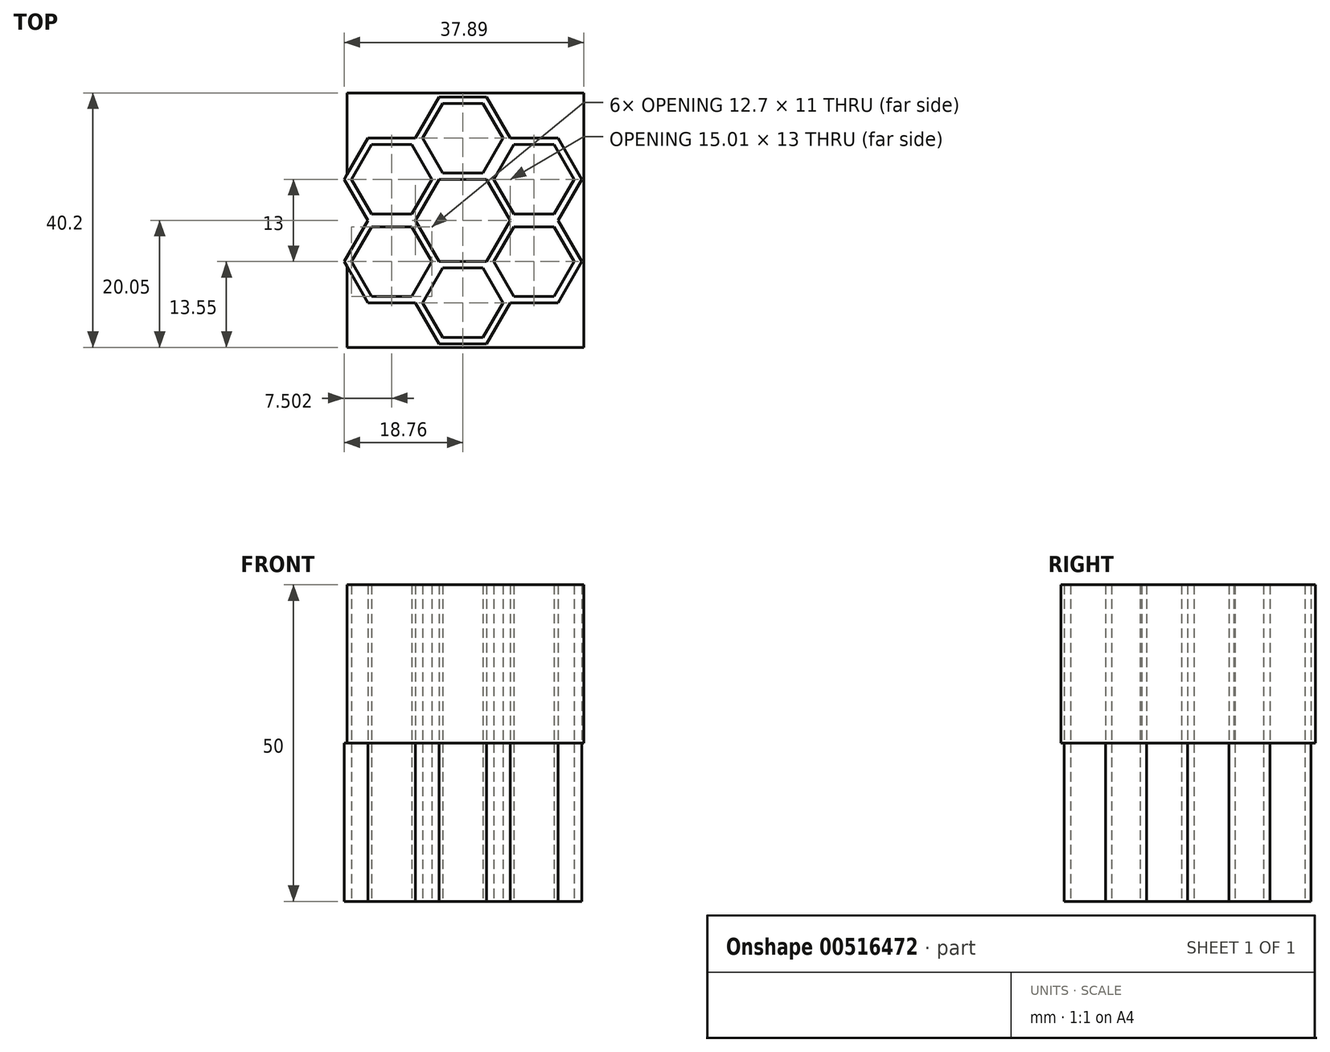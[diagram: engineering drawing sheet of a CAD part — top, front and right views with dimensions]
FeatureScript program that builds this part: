
annotation { "Feature Type Name" : "Feature", "Feature Type Description" : "" }
export const myFeature = defineFeature(function(context is Context, id is Id, definition is map)
    precondition{}
    {
        {
            var Q0;
            Q0=qCreatedBy(makeId("Top.planeOp"),FACE);
            var sketch = newSketch(context, id + "F0", { "sketchPlane" : qUnion([Q0])});
            skLineSegment(sketch, "E0.0", {"start": v(-3.75, 6.5) * mm, "end": v(3.75, 6.5) * mm});
            skLineSegment(sketch, "E0.1", {"start": v(3.75, 6.5) * mm, "end": v(7.5, 0) * mm});
            skLineSegment(sketch, "E0.2", {"start": v(7.5, 0) * mm, "end": v(3.75, -6.5) * mm});
            skLineSegment(sketch, "E0.3", {"start": v(3.75, -6.5) * mm, "end": v(-3.75, -6.5) * mm});
            skLineSegment(sketch, "E0.4", {"start": v(-3.75, -6.5) * mm, "end": v(-7.5, 0) * mm});
            skLineSegment(sketch, "E0.5", {"start": v(-7.5, 0) * mm, "end": v(-3.75, 6.5) * mm});
            skPoint(sketch, "E0.0.midPoint", {"position": v(0, 6.5) * mm});
            skLineSegment(sketch, "E1.0", {"start": v(7.5, 0) * mm, "end": v(15.01, 0) * mm});
            skLineSegment(sketch, "E1.1", {"start": v(15.01, 0) * mm, "end": v(18.76, -6.5) * mm});
            skLineSegment(sketch, "E1.2", {"start": v(18.76, -6.5) * mm, "end": v(15.01, -13) * mm});
            skLineSegment(sketch, "E1.3", {"start": v(15.01, -13) * mm, "end": v(7.5, -13) * mm});
            skLineSegment(sketch, "E1.4", {"start": v(7.5, -13) * mm, "end": v(3.75, -6.5) * mm});
            skLineSegment(sketch, "E1.5", {"start": v(3.75, -6.5) * mm, "end": v(7.5, 0) * mm});
            skPoint(sketch, "E1.0.midPoint", {"position": v(11.26, 0) * mm});
            skLineSegment(sketch, "E2.0", {"start": v(7.5, 13) * mm, "end": v(15.01, 13) * mm});
            skLineSegment(sketch, "E2.1", {"start": v(15.01, 13) * mm, "end": v(18.76, 6.5) * mm});
            skLineSegment(sketch, "E2.2", {"start": v(18.76, 6.5) * mm, "end": v(15.01, 0) * mm});
            skLineSegment(sketch, "E2.3", {"start": v(15.01, 0) * mm, "end": v(7.5, 0) * mm});
            skLineSegment(sketch, "E2.4", {"start": v(7.5, 0) * mm, "end": v(3.75, 6.5) * mm});
            skLineSegment(sketch, "E2.5", {"start": v(3.75, 6.5) * mm, "end": v(7.5, 13) * mm});
            skPoint(sketch, "E2.0.midPoint", {"position": v(11.26, 13) * mm});
            skLineSegment(sketch, "E3.0", {"start": v(-3.75, 19.5) * mm, "end": v(3.75, 19.5) * mm});
            skLineSegment(sketch, "E3.1", {"start": v(3.75, 19.5) * mm, "end": v(7.5, 13) * mm});
            skLineSegment(sketch, "E3.2", {"start": v(7.5, 13) * mm, "end": v(3.75, 6.5) * mm});
            skLineSegment(sketch, "E3.3", {"start": v(3.75, 6.5) * mm, "end": v(-3.75, 6.5) * mm});
            skLineSegment(sketch, "E3.4", {"start": v(-3.75, 6.5) * mm, "end": v(-7.5, 13) * mm});
            skLineSegment(sketch, "E3.5", {"start": v(-7.5, 13) * mm, "end": v(-3.75, 19.5) * mm});
            skPoint(sketch, "E3.0.midPoint", {"position": v(0, 19.5) * mm});
            skLineSegment(sketch, "E4.0", {"start": v(-15.01, 13) * mm, "end": v(-7.5, 13) * mm});
            skLineSegment(sketch, "E4.1", {"start": v(-7.5, 13) * mm, "end": v(-3.75, 6.5) * mm});
            skLineSegment(sketch, "E4.2", {"start": v(-3.75, 6.5) * mm, "end": v(-7.5, 0) * mm});
            skLineSegment(sketch, "E4.3", {"start": v(-7.5, 0) * mm, "end": v(-15.01, 0) * mm});
            skLineSegment(sketch, "E4.4", {"start": v(-15.01, 0) * mm, "end": v(-18.76, 6.5) * mm});
            skLineSegment(sketch, "E4.5", {"start": v(-18.76, 6.5) * mm, "end": v(-15.01, 13) * mm});
            skPoint(sketch, "E4.0.midPoint", {"position": v(-11.26, 13) * mm});
            skLineSegment(sketch, "E5.0", {"start": v(-15.01, 0) * mm, "end": v(-7.5, 0) * mm});
            skLineSegment(sketch, "E5.1", {"start": v(-7.5, 0) * mm, "end": v(-3.75, -6.5) * mm});
            skLineSegment(sketch, "E5.2", {"start": v(-3.75, -6.5) * mm, "end": v(-7.5, -13) * mm});
            skLineSegment(sketch, "E5.3", {"start": v(-7.5, -13) * mm, "end": v(-15.01, -13) * mm});
            skLineSegment(sketch, "E5.4", {"start": v(-15.01, -13) * mm, "end": v(-18.76, -6.5) * mm});
            skLineSegment(sketch, "E5.5", {"start": v(-18.76, -6.5) * mm, "end": v(-15.01, 0) * mm});
            skPoint(sketch, "E5.0.midPoint", {"position": v(-11.26, 0) * mm});
            skLineSegment(sketch, "E6.0", {"start": v(-3.75, -6.5) * mm, "end": v(3.75, -6.5) * mm});
            skLineSegment(sketch, "E6.1", {"start": v(3.75, -6.5) * mm, "end": v(7.5, -13) * mm});
            skLineSegment(sketch, "E6.2", {"start": v(7.5, -13) * mm, "end": v(3.75, -19.5) * mm});
            skLineSegment(sketch, "E6.3", {"start": v(3.75, -19.5) * mm, "end": v(-3.75, -19.5) * mm});
            skLineSegment(sketch, "E6.4", {"start": v(-3.75, -19.5) * mm, "end": v(-7.5, -13) * mm});
            skLineSegment(sketch, "E6.5", {"start": v(-7.5, -13) * mm, "end": v(-3.75, -6.5) * mm});
            skPoint(sketch, "E6.0.midPoint", {"position": v(0, -6.5) * mm});
            skLineSegment(sketch, "E7.0", {"start": v(-14.43, 1) * mm, "end": v(-17.6, 6.5) * mm});
            skLineSegment(sketch, "E7.1", {"start": v(-14.43, 12) * mm, "end": v(-8.08, 12) * mm});
            skLineSegment(sketch, "E7.2", {"start": v(-4.9, 6.5) * mm, "end": v(-8.08, 12) * mm});
            skLineSegment(sketch, "E7.3", {"start": v(-17.6, 6.5) * mm, "end": v(-14.43, 12) * mm});
            skLineSegment(sketch, "E7.4", {"start": v(-8.08, 1) * mm, "end": v(-4.9, 6.5) * mm});
            skLineSegment(sketch, "E7.5", {"start": v(-14.43, 1) * mm, "end": v(-8.08, 1) * mm});
            skLineSegment(sketch, "E8.0", {"start": v(-17.6, -6.5) * mm, "end": v(-14.43, -1) * mm});
            skLineSegment(sketch, "E8.1", {"start": v(-8.08, -1) * mm, "end": v(-4.9, -6.5) * mm});
            skLineSegment(sketch, "E8.2", {"start": v(-8.08, -12) * mm, "end": v(-4.9, -6.5) * mm});
            skLineSegment(sketch, "E8.3", {"start": v(-14.43, -1) * mm, "end": v(-8.08, -1) * mm});
            skLineSegment(sketch, "E8.4", {"start": v(-8.08, -12) * mm, "end": v(-14.43, -12) * mm});
            skLineSegment(sketch, "E8.5", {"start": v(-14.43, -12) * mm, "end": v(-17.6, -6.5) * mm});
            skLineSegment(sketch, "E9.0", {"start": v(6.35, 0) * mm, "end": v(3.18, 5.5) * mm});
            skLineSegment(sketch, "E9.1", {"start": v(-6.35, 0) * mm, "end": v(-3.18, 5.5) * mm});
            skLineSegment(sketch, "E9.2", {"start": v(-6.35, 0) * mm, "end": v(-3.18, -5.5) * mm});
            skLineSegment(sketch, "E9.3", {"start": v(3.18, 5.5) * mm, "end": v(-3.18, 5.5) * mm});
            skLineSegment(sketch, "E9.4", {"start": v(-3.18, -5.5) * mm, "end": v(3.18, -5.5) * mm});
            skLineSegment(sketch, "E9.5", {"start": v(3.18, -5.5) * mm, "end": v(6.35, 0) * mm});
            skLineSegment(sketch, "E10.0", {"start": v(-6.35, 13) * mm, "end": v(-3.18, 18.5) * mm});
            skLineSegment(sketch, "E10.1", {"start": v(3.18, 18.5) * mm, "end": v(6.35, 13) * mm});
            skLineSegment(sketch, "E10.2", {"start": v(3.18, 7.5) * mm, "end": v(6.35, 13) * mm});
            skLineSegment(sketch, "E10.3", {"start": v(-3.18, 18.5) * mm, "end": v(3.18, 18.5) * mm});
            skLineSegment(sketch, "E10.4", {"start": v(3.18, 7.5) * mm, "end": v(-3.18, 7.5) * mm});
            skLineSegment(sketch, "E10.5", {"start": v(-3.18, 7.5) * mm, "end": v(-6.35, 13) * mm});
            skLineSegment(sketch, "E11.0", {"start": v(-3.18, -18.5) * mm, "end": v(-6.35, -13) * mm});
            skLineSegment(sketch, "E11.1", {"start": v(3.18, -7.5) * mm, "end": v(-3.18, -7.5) * mm});
            skLineSegment(sketch, "E11.2", {"start": v(6.35, -13) * mm, "end": v(3.18, -7.5) * mm});
            skLineSegment(sketch, "E11.3", {"start": v(-6.35, -13) * mm, "end": v(-3.18, -7.5) * mm});
            skLineSegment(sketch, "E11.4", {"start": v(6.35, -13) * mm, "end": v(3.18, -18.5) * mm});
            skLineSegment(sketch, "E11.5", {"start": v(3.18, -18.5) * mm, "end": v(-3.18, -18.5) * mm});
            skLineSegment(sketch, "E12.0", {"start": v(4.9, 6.5) * mm, "end": v(8.08, 12) * mm});
            skLineSegment(sketch, "E12.1", {"start": v(14.43, 12) * mm, "end": v(17.6, 6.5) * mm});
            skLineSegment(sketch, "E12.2", {"start": v(17.6, 6.5) * mm, "end": v(14.43, 1) * mm});
            skLineSegment(sketch, "E12.3", {"start": v(8.08, 12) * mm, "end": v(14.43, 12) * mm});
            skLineSegment(sketch, "E12.4", {"start": v(8.08, 1) * mm, "end": v(14.43, 1) * mm});
            skLineSegment(sketch, "E12.5", {"start": v(8.08, 1) * mm, "end": v(4.9, 6.5) * mm});
            skLineSegment(sketch, "E13.0", {"start": v(4.9, -6.5) * mm, "end": v(8.08, -1) * mm});
            skLineSegment(sketch, "E13.1", {"start": v(14.43, -1) * mm, "end": v(17.6, -6.5) * mm});
            skLineSegment(sketch, "E13.2", {"start": v(17.6, -6.5) * mm, "end": v(14.43, -12) * mm});
            skLineSegment(sketch, "E13.3", {"start": v(8.08, -1) * mm, "end": v(14.43, -1) * mm});
            skLineSegment(sketch, "E13.4", {"start": v(14.43, -12) * mm, "end": v(8.08, -12) * mm});
            skLineSegment(sketch, "E13.5", {"start": v(8.08, -12) * mm, "end": v(4.9, -6.5) * mm});
            skSolve(sketch);
        }
        {
            var Q0;
            Q0=qSketchRegion(id+"F0",true);
            extrude(context, id + "F1", {"entities" : qUnion([Q0]), "depth" : 25 * mm, "offsetDistance" : 25 * mm});
        }
        {
            var Q0;
            Q0=makeQuery(id+"F1.opExtrude","CAP_FACE",FACE,{"disambiguationData":[OSD([sQuery(id+"F0.wireOp",EDGE,"E1.1"),sQuery(id+"F0.wireOp",EDGE,"E1.2"),sQuery(id+"F0.wireOp",EDGE,"E1.3"),sQuery(id+"F0.wireOp",EDGE,"E1.5"),sQuery(id+"F0.wireOp",EDGE,"E2.0"),sQuery(id+"F0.wireOp",EDGE,"E2.1"),sQuery(id+"F0.wireOp",EDGE,"E2.2"),sQuery(id+"F0.wireOp",EDGE,"E2.4"),sQuery(id+"F0.wireOp",EDGE,"E3.0"),sQuery(id+"F0.wireOp",EDGE,"E3.1"),sQuery(id+"F0.wireOp",EDGE,"E3.3"),sQuery(id+"F0.wireOp",EDGE,"E3.5"),sQuery(id+"F0.wireOp",EDGE,"E4.0"),sQuery(id+"F0.wireOp",EDGE,"E4.2"),sQuery(id+"F0.wireOp",EDGE,"E4.4"),sQuery(id+"F0.wireOp",EDGE,"E4.5"),sQuery(id+"F0.wireOp",EDGE,"E5.1"),sQuery(id+"F0.wireOp",EDGE,"E5.3"),sQuery(id+"F0.wireOp",EDGE,"E5.4"),sQuery(id+"F0.wireOp",EDGE,"E5.5"),sQuery(id+"F0.wireOp",EDGE,"E6.0"),sQuery(id+"F0.wireOp",EDGE,"E6.2"),sQuery(id+"F0.wireOp",EDGE,"E6.3"),sQuery(id+"F0.wireOp",EDGE,"E6.4"),sQuery(id+"F0.wireOp",EDGE,"E7.0"),sQuery(id+"F0.wireOp",EDGE,"E7.1"),sQuery(id+"F0.wireOp",EDGE,"E7.2"),sQuery(id+"F0.wireOp",EDGE,"E7.3"),sQuery(id+"F0.wireOp",EDGE,"E7.4"),sQuery(id+"F0.wireOp",EDGE,"E7.5"),sQuery(id+"F0.wireOp",EDGE,"E8.0"),sQuery(id+"F0.wireOp",EDGE,"E8.1"),sQuery(id+"F0.wireOp",EDGE,"E8.2"),sQuery(id+"F0.wireOp",EDGE,"E8.3"),sQuery(id+"F0.wireOp",EDGE,"E8.4"),sQuery(id+"F0.wireOp",EDGE,"E8.5"),sQuery(id+"F0.wireOp",EDGE,"E10.0"),sQuery(id+"F0.wireOp",EDGE,"E10.1"),sQuery(id+"F0.wireOp",EDGE,"E10.2"),sQuery(id+"F0.wireOp",EDGE,"E10.3"),sQuery(id+"F0.wireOp",EDGE,"E10.4"),sQuery(id+"F0.wireOp",EDGE,"E10.5"),sQuery(id+"F0.wireOp",EDGE,"E11.0"),sQuery(id+"F0.wireOp",EDGE,"E11.1"),sQuery(id+"F0.wireOp",EDGE,"E11.2"),sQuery(id+"F0.wireOp",EDGE,"E11.3"),sQuery(id+"F0.wireOp",EDGE,"E11.4"),sQuery(id+"F0.wireOp",EDGE,"E11.5"),sQuery(id+"F0.wireOp",EDGE,"E12.0"),sQuery(id+"F0.wireOp",EDGE,"E12.1"),sQuery(id+"F0.wireOp",EDGE,"E12.2"),sQuery(id+"F0.wireOp",EDGE,"E12.3"),sQuery(id+"F0.wireOp",EDGE,"E12.4"),sQuery(id+"F0.wireOp",EDGE,"E12.5"),sQuery(id+"F0.wireOp",EDGE,"E13.0"),sQuery(id+"F0.wireOp",EDGE,"E13.1"),sQuery(id+"F0.wireOp",EDGE,"E13.2"),sQuery(id+"F0.wireOp",EDGE,"E13.3"),sQuery(id+"F0.wireOp",EDGE,"E13.4"),sQuery(id+"F0.wireOp",EDGE,"E13.5")])],"isStart":false});
            var sketch = newSketch(context, id + "F2", { "sketchPlane" : qUnion([Q0])});
            skSolve(sketch);
        }
        {
            var Q0;
            Q0=makeQuery(id+"F2.imprint","IMPRINT",FACE,{"disambiguationData":[TD([[makeQuery(id+"F2.imprint","IMPRINT",EDGE,{"derivedFrom":makeQuery(id+"F1.opExtrude","CAP_EDGE",EDGE,{"disambiguationData":[OSD([sQuery(id+"F0.wireOp",EDGE,"E1.1")])],"isStart":false})}),-1.0]])]});
            extrude(context, id + "F3", {"entities" : qUnion([Q0]), "operationType" : NewBodyOperationType.ADD, "oppositeDirection" : true, "depth" : 25 * mm, "offsetDistance" : 25 * mm});
        }
        {
            var Q0;
            Q0=makeQuery(id+"F1.opExtrude","CAP_FACE",FACE,{"disambiguationData":[OSD([sQuery(id+"F0.wireOp",EDGE,"E1.1"),sQuery(id+"F0.wireOp",EDGE,"E1.2"),sQuery(id+"F0.wireOp",EDGE,"E1.3"),sQuery(id+"F0.wireOp",EDGE,"E1.5"),sQuery(id+"F0.wireOp",EDGE,"E2.0"),sQuery(id+"F0.wireOp",EDGE,"E2.1"),sQuery(id+"F0.wireOp",EDGE,"E2.2"),sQuery(id+"F0.wireOp",EDGE,"E2.4"),sQuery(id+"F0.wireOp",EDGE,"E3.0"),sQuery(id+"F0.wireOp",EDGE,"E3.1"),sQuery(id+"F0.wireOp",EDGE,"E3.3"),sQuery(id+"F0.wireOp",EDGE,"E3.5"),sQuery(id+"F0.wireOp",EDGE,"E4.0"),sQuery(id+"F0.wireOp",EDGE,"E4.2"),sQuery(id+"F0.wireOp",EDGE,"E4.4"),sQuery(id+"F0.wireOp",EDGE,"E4.5"),sQuery(id+"F0.wireOp",EDGE,"E5.1"),sQuery(id+"F0.wireOp",EDGE,"E5.3"),sQuery(id+"F0.wireOp",EDGE,"E5.4"),sQuery(id+"F0.wireOp",EDGE,"E5.5"),sQuery(id+"F0.wireOp",EDGE,"E6.0"),sQuery(id+"F0.wireOp",EDGE,"E6.2"),sQuery(id+"F0.wireOp",EDGE,"E6.3"),sQuery(id+"F0.wireOp",EDGE,"E6.4"),sQuery(id+"F0.wireOp",EDGE,"E7.0"),sQuery(id+"F0.wireOp",EDGE,"E7.1"),sQuery(id+"F0.wireOp",EDGE,"E7.2"),sQuery(id+"F0.wireOp",EDGE,"E7.3"),sQuery(id+"F0.wireOp",EDGE,"E7.4"),sQuery(id+"F0.wireOp",EDGE,"E7.5"),sQuery(id+"F0.wireOp",EDGE,"E8.0"),sQuery(id+"F0.wireOp",EDGE,"E8.1"),sQuery(id+"F0.wireOp",EDGE,"E8.2"),sQuery(id+"F0.wireOp",EDGE,"E8.3"),sQuery(id+"F0.wireOp",EDGE,"E8.4"),sQuery(id+"F0.wireOp",EDGE,"E8.5"),sQuery(id+"F0.wireOp",EDGE,"E10.0"),sQuery(id+"F0.wireOp",EDGE,"E10.1"),sQuery(id+"F0.wireOp",EDGE,"E10.2"),sQuery(id+"F0.wireOp",EDGE,"E10.3"),sQuery(id+"F0.wireOp",EDGE,"E10.4"),sQuery(id+"F0.wireOp",EDGE,"E10.5"),sQuery(id+"F0.wireOp",EDGE,"E11.0"),sQuery(id+"F0.wireOp",EDGE,"E11.1"),sQuery(id+"F0.wireOp",EDGE,"E11.2"),sQuery(id+"F0.wireOp",EDGE,"E11.3"),sQuery(id+"F0.wireOp",EDGE,"E11.4"),sQuery(id+"F0.wireOp",EDGE,"E11.5"),sQuery(id+"F0.wireOp",EDGE,"E12.0"),sQuery(id+"F0.wireOp",EDGE,"E12.1"),sQuery(id+"F0.wireOp",EDGE,"E12.2"),sQuery(id+"F0.wireOp",EDGE,"E12.3"),sQuery(id+"F0.wireOp",EDGE,"E12.4"),sQuery(id+"F0.wireOp",EDGE,"E12.5"),sQuery(id+"F0.wireOp",EDGE,"E13.0"),sQuery(id+"F0.wireOp",EDGE,"E13.1"),sQuery(id+"F0.wireOp",EDGE,"E13.2"),sQuery(id+"F0.wireOp",EDGE,"E13.3"),sQuery(id+"F0.wireOp",EDGE,"E13.4"),sQuery(id+"F0.wireOp",EDGE,"E13.5")])],"isStart":false});
            var sketch = newSketch(context, id + "F4", { "sketchPlane" : qUnion([Q0])});
            skSolve(sketch);
        }
        {
            var Q0;
            Q0=makeQuery(id+"F4.imprint","IMPRINT",FACE,{"disambiguationData":[TD([[makeQuery(id+"F4.imprint","IMPRINT",EDGE,{"derivedFrom":makeQuery(id+"F1.opExtrude","CAP_EDGE",EDGE,{"disambiguationData":[OSD([sQuery(id+"F0.wireOp",EDGE,"E1.1")])],"isStart":false})}),-1.0]])]});
            var sketch = newSketch(context, id + "F5", { "sketchPlane" : qUnion([Q0])});
            skLineSegment(sketch, "E14.bottom", {"start": v(-18.32, 20.15) * mm, "end": v(8.54, 20.15) * mm});
            skLineSegment(sketch, "E14.top", {"start": v(-18.32, -20.05) * mm, "end": v(8.54, -20.05) * mm});
            skLineSegment(sketch, "E14.left", {"start": v(-18.32, 20.15) * mm, "end": v(-18.32, -20.05) * mm});
            skLineSegment(sketch, "E14.right", {"start": v(8.54, 20.15) * mm, "end": v(8.54, -20.05) * mm});
            skLineSegment(sketch, "E15.bottom", {"start": v(8.54, 20.15) * mm, "end": v(19.13, 20.15) * mm});
            skLineSegment(sketch, "E15.top", {"start": v(8.54, -20.05) * mm, "end": v(19.13, -20.05) * mm});
            skLineSegment(sketch, "E15.right", {"start": v(19.13, 20.15) * mm, "end": v(19.13, -20.05) * mm});
            skLineSegment(sketch, "E16.bottom", {"start": v(-18.32, 6.67) * mm, "end": v(-18.32, 6.67) * mm});
            skLineSegment(sketch, "E16.top", {"start": v(-18.32, 20.15) * mm, "end": v(-18.32, 20.15) * mm});
            skLineSegment(sketch, "E16.left", {"start": v(-18.32, 6.67) * mm, "end": v(-18.32, 20.15) * mm});
            skLineSegment(sketch, "E16.right", {"start": v(-18.32, 6.67) * mm, "end": v(-18.32, 20.15) * mm});
            skLineSegment(sketch, "E17.bottom", {"start": v(-18.45, 20.15) * mm, "end": v(-18.32, 20.15) * mm});
            skLineSegment(sketch, "E17.top", {"start": v(-18.45, -19.28) * mm, "end": v(-18.32, -19.28) * mm});
            skLineSegment(sketch, "E17.left", {"start": v(-18.45, 20.15) * mm, "end": v(-18.45, -19.28) * mm});
            skLineSegment(sketch, "E17.right", {"start": v(-18.32, 20.15) * mm, "end": v(-18.32, -19.28) * mm});
            skSolve(sketch);
        }
        {
            var Q0;
            {var subQ0=sQuery(id+"F5.wireOp",EDGE,"E17.right");var subQ1=makeQuery(id+"F4.imprint","IMPRINT",EDGE,{"derivedFrom":makeQuery(id+"F1.opExtrude","CAP_EDGE",EDGE,{"disambiguationData":[OSD([sQuery(id+"F0.wireOp",EDGE,"E4.4")])],"isStart":false})});var subQ2=makeQuery(id+"F5.imprint","INTERSECT",VERTEX,{"derivedFrom":[subQ1,subQ0]});Q0=makeQuery(id+"F5.imprint","IMPRINT",FACE,{"disambiguationData":[TD([[makeQuery(id+"F5.imprint","IMPRINT",EDGE,{"disambiguationData":[TD([[subQ2,-1.0]])],"derivedFrom":subQ0}),1.0]])]});}
            var Q1;
            Q1=makeQuery(id+"F4.imprint","IMPRINT",FACE,{"disambiguationData":[TD([[makeQuery(id+"F4.imprint","IMPRINT",EDGE,{"derivedFrom":makeQuery(id+"F1.opExtrude","CAP_EDGE",EDGE,{"disambiguationData":[OSD([sQuery(id+"F0.wireOp",EDGE,"E7.0")])],"isStart":false})}),-1.0]])]});
            var Q2;
            Q2=makeQuery(id+"F4.imprint","IMPRINT",FACE,{"disambiguationData":[TD([[makeQuery(id+"F4.imprint","IMPRINT",EDGE,{"derivedFrom":makeQuery(id+"F1.opExtrude","CAP_EDGE",EDGE,{"disambiguationData":[OSD([sQuery(id+"F0.wireOp",EDGE,"E8.0")])],"isStart":false})}),-1.0]])]});
            var Q3;
            Q3=makeQuery(id+"F4.imprint","IMPRINT",FACE,{"disambiguationData":[TD([[makeQuery(id+"F4.imprint","IMPRINT",EDGE,{"derivedFrom":makeQuery(id+"F1.opExtrude","CAP_EDGE",EDGE,{"disambiguationData":[OSD([sQuery(id+"F0.wireOp",EDGE,"E1.5")])],"isStart":false})}),1.0]])]});
            var Q4;
            Q4=makeQuery(id+"F4.imprint","IMPRINT",FACE,{"disambiguationData":[TD([[makeQuery(id+"F4.imprint","IMPRINT",EDGE,{"derivedFrom":makeQuery(id+"F1.opExtrude","CAP_EDGE",EDGE,{"disambiguationData":[OSD([sQuery(id+"F0.wireOp",EDGE,"E11.0")])],"isStart":false})}),-1.0]])]});
            var Q5;
            {var subQ5=sQuery(id+"F5.wireOp",EDGE,"E14.top");Q5=makeQuery(id+"F5.imprint","IMPRINT",FACE,{"disambiguationData":[TD([[makeQuery(id+"F5.imprint","IMPRINT",EDGE,{"derivedFrom":subQ5}),1.0]])]});}
            var Q6;
            {var subQ5=sQuery(id+"F5.wireOp",EDGE,"E15.bottom");Q6=makeQuery(id+"F5.imprint","IMPRINT",FACE,{"disambiguationData":[TD([[makeQuery(id+"F5.imprint","IMPRINT",EDGE,{"derivedFrom":subQ5}),-1.0]])]});}
            var Q7;
            Q7=makeQuery(id+"F4.imprint","IMPRINT",FACE,{"disambiguationData":[TD([[makeQuery(id+"F4.imprint","IMPRINT",EDGE,{"derivedFrom":makeQuery(id+"F1.opExtrude","CAP_EDGE",EDGE,{"disambiguationData":[OSD([sQuery(id+"F0.wireOp",EDGE,"E13.0")])],"isStart":false})}),-1.0]])]});
            var Q8;
            Q8=makeQuery(id+"F4.imprint","IMPRINT",FACE,{"disambiguationData":[TD([[makeQuery(id+"F4.imprint","IMPRINT",EDGE,{"derivedFrom":makeQuery(id+"F1.opExtrude","CAP_EDGE",EDGE,{"disambiguationData":[OSD([sQuery(id+"F0.wireOp",EDGE,"E12.0")])],"isStart":false})}),-1.0]])]});
            var Q9;
            {var subQ1=sQuery(id+"F5.wireOp",EDGE,"E14.bottom");Q9=makeQuery(id+"F5.imprint","IMPRINT",FACE,{"disambiguationData":[TD([[makeQuery(id+"F5.imprint","IMPRINT",EDGE,{"derivedFrom":subQ1}),-1.0]])]});}
            var Q10;
            Q10=makeQuery(id+"F4.imprint","IMPRINT",FACE,{"disambiguationData":[TD([[makeQuery(id+"F4.imprint","IMPRINT",EDGE,{"derivedFrom":makeQuery(id+"F1.opExtrude","CAP_EDGE",EDGE,{"disambiguationData":[OSD([sQuery(id+"F0.wireOp",EDGE,"E10.0")])],"isStart":false})}),-1.0]])]});
            extrude(context, id + "F6", {"entities" : qUnion([Q0, Q1, Q2, Q3, Q4, Q5, Q6, Q7, Q8, Q9, Q10]), "depth" : 25 * mm, "offsetDistance" : 25 * mm});
        }
    });
